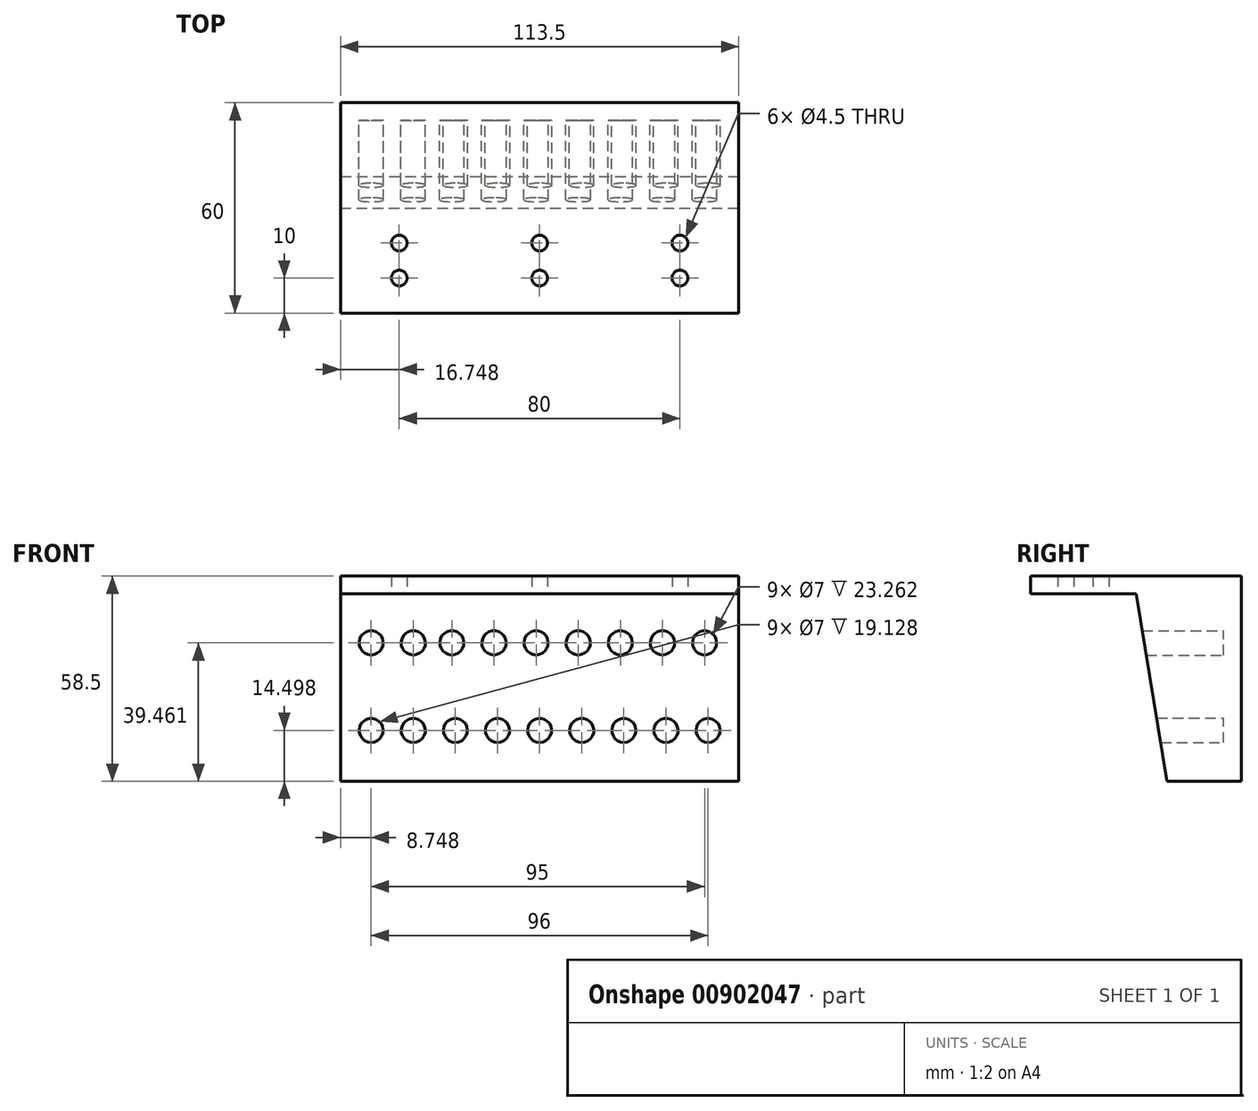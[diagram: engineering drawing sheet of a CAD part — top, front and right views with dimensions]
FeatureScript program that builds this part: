
annotation { "Feature Type Name" : "Feature", "Feature Type Description" : "" }
export const myFeature = defineFeature(function(context is Context, id is Id, definition is map)
    precondition{}
    {
        {
            var Q0;
            Q0=qCreatedBy(makeId("Front.planeOp"),FACE);
            var sketch = newSketch(context, id + "F0", { "sketchPlane" : qUnion([Q0])});
            skLineSegment(sketch, "E0.bottom", {"start": v(-82.73, 51.75) * mm, "end": v(30.77, 51.75) * mm});
            skLineSegment(sketch, "E0.top", {"start": v(-82.73, -1.75) * mm, "end": v(30.77, -1.75) * mm});
            skLineSegment(sketch, "E0.left", {"start": v(-82.73, 51.75) * mm, "end": v(-82.73, -1.75) * mm});
            skLineSegment(sketch, "E0.right", {"start": v(30.77, 51.75) * mm, "end": v(30.77, -1.75) * mm});
            skLineSegment(sketch, "E1", {"start": v(30.77, 37.71) * mm, "end": v(-82.73, 37.71) * mm});
            skLineSegment(sketch, "E2", {"start": v(-82.73, 37.71) * mm, "end": v(-82.73, 12.75) * mm});
            skLineSegment(sketch, "E3", {"start": v(-82.73, 12.75) * mm, "end": v(30.77, 12.75) * mm});
            skCircle(sketch, "E4", {"center": v(-2.98, 37.71) * mm, "radius": 3.5 * mm});
            skCircle(sketch, "E5", {"center": v(-14.98, 37.71) * mm, "radius": 3.5 * mm});
            skCircle(sketch, "E6", {"center": v(-26.98, 37.71) * mm, "radius": 3.5 * mm});
            skCircle(sketch, "E7", {"center": v(-38.98, 37.71) * mm, "radius": 3.5 * mm});
            skCircle(sketch, "E8", {"center": v(-50.98, 37.71) * mm, "radius": 3.5 * mm});
            skCircle(sketch, "E9", {"center": v(-61.98, 37.71) * mm, "radius": 3.5 * mm});
            skCircle(sketch, "E10", {"center": v(-73.98, 37.71) * mm, "radius": 3.5 * mm});
            skCircle(sketch, "E11", {"center": v(22.02, 12.75) * mm, "radius": 3.5 * mm});
            skCircle(sketch, "E12", {"center": v(10.02, 12.75) * mm, "radius": 3.5 * mm});
            skCircle(sketch, "E13", {"center": v(-1.98, 12.75) * mm, "radius": 3.5 * mm});
            skCircle(sketch, "E14", {"center": v(-13.98, 12.75) * mm, "radius": 3.5 * mm});
            skCircle(sketch, "E15", {"center": v(-25.98, 12.75) * mm, "radius": 3.5 * mm});
            skCircle(sketch, "E16", {"center": v(-37.98, 12.75) * mm, "radius": 3.5 * mm});
            skCircle(sketch, "E17", {"center": v(-49.98, 12.75) * mm, "radius": 3.5 * mm});
            skCircle(sketch, "E18", {"center": v(-61.98, 12.75) * mm, "radius": 3.5 * mm});
            skCircle(sketch, "E19", {"center": v(-73.98, 12.75) * mm, "radius": 3.5 * mm});
            skCircle(sketch, "E20", {"center": v(9.02, 37.71) * mm, "radius": 3.5 * mm});
            skCircle(sketch, "E21", {"center": v(21.02, 37.71) * mm, "radius": 3.5 * mm});
            skSolve(sketch);
        }
        {
            var Q0;
            {var subQ15=sQuery(id+"F0.wireOp",EDGE,"E0.left");var subQ21=sQuery(id+"F0.wireOp",EDGE,"E1");var subQ30=makeQuery(id+"F0.imprint","INTERSECT",VERTEX,{"derivedFrom":[subQ15,subQ21]});var subQ82=sQuery(id+"F0.wireOp",EDGE,"E0.top");var subQ83=sQuery(id+"F0.wireOp",EDGE,"E0.bottom");Q0=qUnion([makeQuery(id+"F0.imprint","IMPRINT",FACE,{"disambiguationData":[TD([[makeQuery(id+"F0.imprint","IMPRINT",EDGE,{"derivedFrom":subQ83}),-1.0]])]}),makeQuery(id+"F0.imprint","IMPRINT",FACE,{"disambiguationData":[TD([[makeQuery(id+"F0.imprint","IMPRINT",EDGE,{"derivedFrom":subQ82}),1.0]])]}),makeQuery(id+"F0.imprint","IMPRINT",FACE,{"disambiguationData":[TD([[makeQuery(id+"F0.imprint","IMPRINT",EDGE,{"disambiguationData":[TD([[subQ30,-1.0]])],"derivedFrom":subQ15}),1.0]])]})]);}
            extrude(context, id + "F1", {"entities" : qUnion([Q0]), "depth" : 25 * mm, "offsetDistance" : 25 * mm});
        }
        {
            var Q0;
            Q0=makeQuery(id+"F1.opExtrude","CAP_FACE",FACE,{"disambiguationData":[OSD([sQuery(id+"F0.wireOp",EDGE,"E0.bottom"),sQuery(id+"F0.wireOp",EDGE,"E0.top"),sQuery(id+"F0.wireOp",EDGE,"E0.left"),sQuery(id+"F0.wireOp",EDGE,"E0.right"),sQuery(id+"F0.wireOp",EDGE,"E4"),sQuery(id+"F0.wireOp",EDGE,"E5"),sQuery(id+"F0.wireOp",EDGE,"E6"),sQuery(id+"F0.wireOp",EDGE,"E7"),sQuery(id+"F0.wireOp",EDGE,"E8"),sQuery(id+"F0.wireOp",EDGE,"E9"),sQuery(id+"F0.wireOp",EDGE,"E10"),sQuery(id+"F0.wireOp",EDGE,"E11"),sQuery(id+"F0.wireOp",EDGE,"E12"),sQuery(id+"F0.wireOp",EDGE,"E13"),sQuery(id+"F0.wireOp",EDGE,"E14"),sQuery(id+"F0.wireOp",EDGE,"E15"),sQuery(id+"F0.wireOp",EDGE,"E16"),sQuery(id+"F0.wireOp",EDGE,"E17"),sQuery(id+"F0.wireOp",EDGE,"E18"),sQuery(id+"F0.wireOp",EDGE,"E19"),sQuery(id+"F0.wireOp",EDGE,"E20"),sQuery(id+"F0.wireOp",EDGE,"E21")])],"isStart":true});
            var sketch = newSketch(context, id + "F2", { "sketchPlane" : qUnion([Q0])});
            skLineSegment(sketch, "E22.bottom", {"start": v(-30.77, 51.75) * mm, "end": v(82.73, 51.75) * mm});
            skLineSegment(sketch, "E22.top", {"start": v(-30.77, -1.75) * mm, "end": v(82.73, -1.75) * mm});
            skLineSegment(sketch, "E22.left", {"start": v(-30.77, 51.75) * mm, "end": v(-30.77, -1.75) * mm});
            skLineSegment(sketch, "E22.right", {"start": v(82.73, 51.75) * mm, "end": v(82.73, -1.75) * mm});
            skSolve(sketch);
        }
        {
            var Q0;
            Q0=qSketchRegion(id+"F2",true);
            extrude(context, id + "F3", {"entities" : qUnion([Q0]), "operationType" : NewBodyOperationType.ADD, "depth" : 5 * mm, "offsetDistance" : 25 * mm});
        }
        {
            var Q0;
            Q0=makeQuery(id+"F3.boolean.opBoolean","MERGE",FACE,{"derivedFrom":[makeQuery(id+"F1.opExtrude","SWEPT_FACE",FACE,{"disambiguationData":[OSD([sQuery(id+"F0.wireOp",EDGE,"E0.left")])]}),makeQuery(id+"F3.opExtrude","SWEPT_FACE",FACE,{"disambiguationData":[OSD([sQuery(id+"F2.wireOp",EDGE,"E22.right")])]})]});
            var sketch = newSketch(context, id + "F4", { "sketchPlane" : qUnion([Q0])});
            skLineSegment(sketch, "E23", {"start": v(25, 51.75) * mm, "end": v(16.14, -1.75) * mm});
            skLineSegment(sketch, "E24", {"start": v(16.14, -1.75) * mm, "end": v(25, -1.75) * mm});
            skLineSegment(sketch, "E25", {"start": v(25, -1.75) * mm, "end": v(25, 51.75) * mm});
            skSolve(sketch);
        }
        {
            var Q0;
            Q0=qSketchRegion(id+"F4",true);
            extrude(context, id + "F5", {"entities" : qUnion([Q0]), "operationType" : NewBodyOperationType.REMOVE, "oppositeDirection" : true, "depth" : 133.9 * mm, "offsetDistance" : 25 * mm});
        }
        {
            var Q0;
            Q0=makeQuery(id+"F3.boolean.opBoolean","MERGE",FACE,{"derivedFrom":[makeQuery(id+"F1.opExtrude","SWEPT_FACE",FACE,{"disambiguationData":[OSD([sQuery(id+"F0.wireOp",EDGE,"E0.bottom")])]}),makeQuery(id+"F3.opExtrude","SWEPT_FACE",FACE,{"disambiguationData":[OSD([sQuery(id+"F2.wireOp",EDGE,"E22.bottom")])]})]});
            var sketch = newSketch(context, id + "F6", { "sketchPlane" : qUnion([Q0])});
            skLineSegment(sketch, "E26.bottom", {"start": v(30.77, 5) * mm, "end": v(-82.73, 5) * mm});
            skLineSegment(sketch, "E26.top", {"start": v(30.77, -55) * mm, "end": v(-82.73, -55) * mm});
            skLineSegment(sketch, "E26.left", {"start": v(30.77, 5) * mm, "end": v(30.77, -55) * mm});
            skLineSegment(sketch, "E26.right", {"start": v(-82.73, 5) * mm, "end": v(-82.73, -55) * mm});
            skSolve(sketch);
        }
        {
            var Q0;
            Q0=qSketchRegion(id+"F6",true);
            extrude(context, id + "F7", {"entities" : qUnion([Q0]), "operationType" : NewBodyOperationType.ADD, "depth" : 5 * mm, "offsetDistance" : 25 * mm});
        }
        {
            var Q0;
            Q0=makeQuery(id+"F7.opExtrude","CAP_FACE",FACE,{"disambiguationData":[OSD([sQuery(id+"F6.wireOp",EDGE,"E26.bottom"),sQuery(id+"F6.wireOp",EDGE,"E26.top"),sQuery(id+"F6.wireOp",EDGE,"E26.left"),sQuery(id+"F6.wireOp",EDGE,"E26.right")])],"isStart":true});
            var sketch = newSketch(context, id + "F8", { "sketchPlane" : qUnion([Q0])});
            skLineSegment(sketch, "E27", {"start": v(-82.73, 45) * mm, "end": v(30.77, 45) * mm});
            skLineSegment(sketch, "E28", {"start": v(-82.73, 35) * mm, "end": v(30.77, 35) * mm});
            skCircle(sketch, "E29", {"center": v(-65.98, 45) * mm, "radius": 2.25 * mm});
            skCircle(sketch, "E30", {"center": v(-25.98, 45) * mm, "radius": 2.25 * mm});
            skCircle(sketch, "E31", {"center": v(14.02, 45) * mm, "radius": 2.25 * mm});
            skCircle(sketch, "E32", {"center": v(-25.98, 35) * mm, "radius": 2.25 * mm});
            skCircle(sketch, "E33", {"center": v(-65.98, 35) * mm, "radius": 2.25 * mm});
            skCircle(sketch, "E34", {"center": v(14.02, 35) * mm, "radius": 2.25 * mm});
            skSolve(sketch);
        }
        {
            var Q0;
            Q0=qSketchRegion(id+"F8",true);
            extrude(context, id + "F9", {"entities" : qUnion([Q0]), "operationType" : NewBodyOperationType.REMOVE, "oppositeDirection" : true, "depth" : 25 * mm, "offsetDistance" : 25 * mm});
        }
    });
